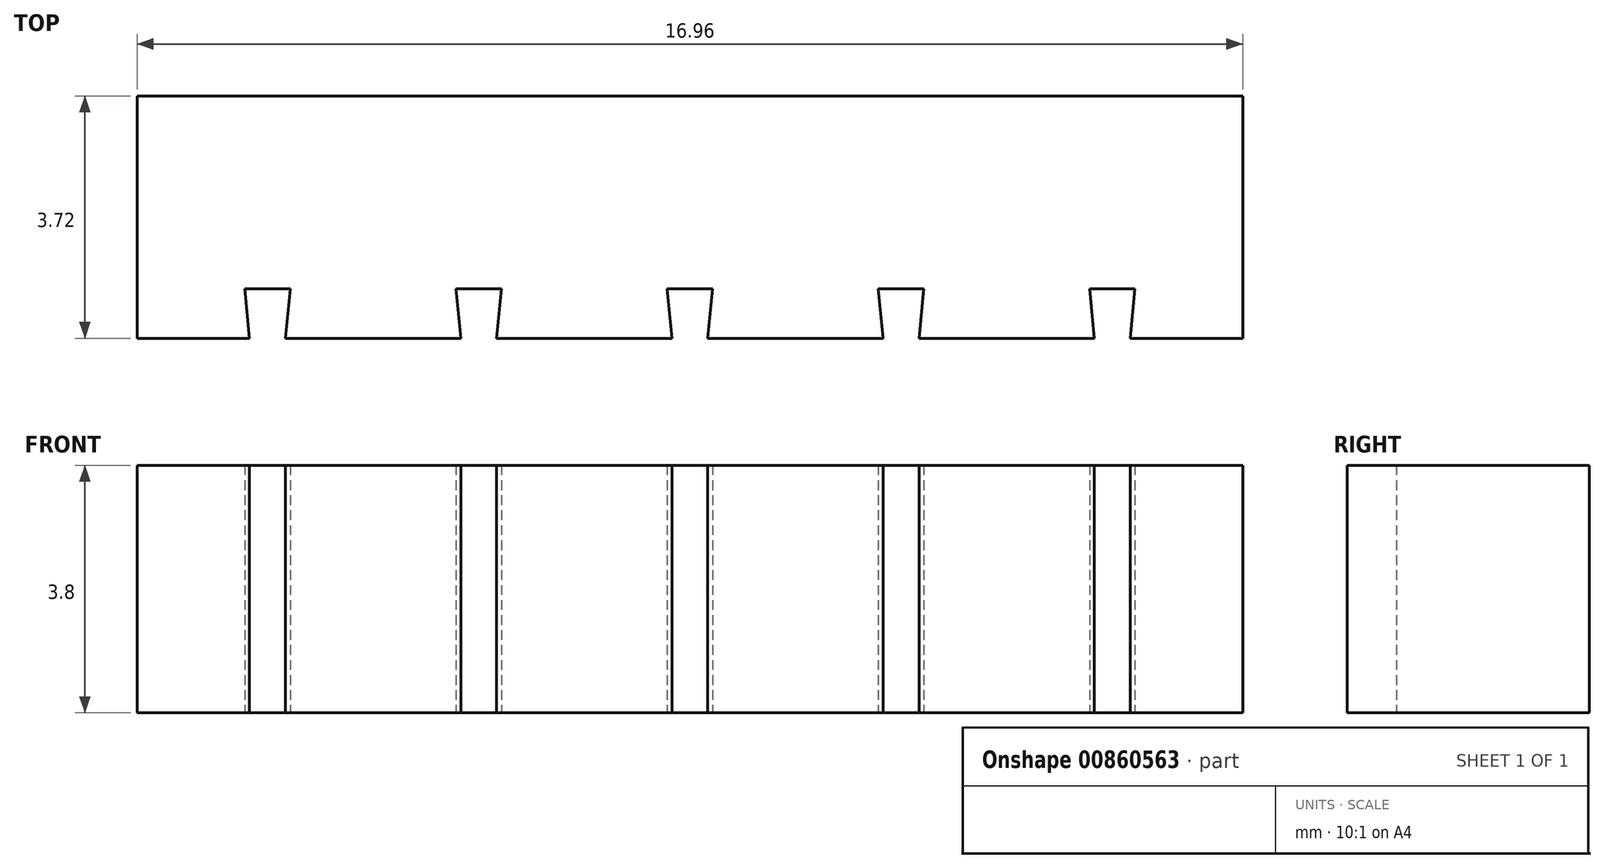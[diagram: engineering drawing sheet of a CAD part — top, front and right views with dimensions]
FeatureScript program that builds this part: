
annotation { "Feature Type Name" : "Feature", "Feature Type Description" : "" }
export const myFeature = defineFeature(function(context is Context, id is Id, definition is map)
    precondition{}
    {
        {
            var Q0;
            Q0=qCreatedBy(makeId("Top.planeOp"),FACE);
            var sketch = newSketch(context, id + "F0", { "sketchPlane" : qUnion([Q0])});
            skLineSegment(sketch, "E0.bottom", {"start": v(0, 0) * mm, "end": v(16.96, 0) * mm});
            skLineSegment(sketch, "E0.top", {"start": v(0, 3.72) * mm, "end": v(16.96, 3.72) * mm});
            skLineSegment(sketch, "E0.left", {"start": v(0, 0) * mm, "end": v(0, 3.72) * mm});
            skLineSegment(sketch, "E0.right", {"start": v(16.96, 0) * mm, "end": v(16.96, 3.72) * mm});
            skLineSegment(sketch, "E1", {"start": v(2, 0) * mm, "end": v(2, 3.72) * mm, "construction": true});
            skLineSegment(sketch, "E2", {"start": v(5.24, 0) * mm, "end": v(5.24, 3.72) * mm, "construction": true});
            skLineSegment(sketch, "E3", {"start": v(8.48, 3.72) * mm, "end": v(8.48, 0) * mm, "construction": true});
            skLineSegment(sketch, "E4", {"start": v(11.72, 0) * mm, "end": v(11.72, 3.72) * mm, "construction": true});
            skLineSegment(sketch, "E5", {"start": v(14.96, 3.72) * mm, "end": v(14.96, 0) * mm, "construction": true});
            skLineSegment(sketch, "E6", {"start": v(5.24, 0) * mm, "end": v(8.48, 0) * mm});
            skLineSegment(sketch, "E7", {"start": v(11.72, 0) * mm, "end": v(14.96, 0) * mm});
            skLineSegment(sketch, "E8", {"start": v(2, 0) * mm, "end": v(5.24, 0) * mm});
            skLineSegment(sketch, "E9", {"start": v(8.48, 0) * mm, "end": v(11.72, 0) * mm});
            skLineSegment(sketch, "E10", {"start": v(0, 0) * mm, "end": v(2, 0) * mm});
            skLineSegment(sketch, "E11", {"start": v(14.96, 0) * mm, "end": v(16.96, 0) * mm});
            skLineSegment(sketch, "E12", {"start": v(0, 0.76) * mm, "end": v(16.96, 0.76) * mm, "construction": true});
            skLineSegment(sketch, "E13", {"start": v(1.73, 0) * mm, "end": v(1.65, 0.76) * mm});
            skLineSegment(sketch, "E14", {"start": v(1.65, 0.76) * mm, "end": v(2, 0.76) * mm});
            skLineSegment(sketch, "E15", {"start": v(2, 0.76) * mm, "end": v(2.35, 0.76) * mm});
            skLineSegment(sketch, "E16", {"start": v(2.35, 0.76) * mm, "end": v(2.27, 0) * mm});
            skLineSegment(sketch, "E17", {"start": v(4.97, 0) * mm, "end": v(4.9, 0.76) * mm});
            skLineSegment(sketch, "E18", {"start": v(4.9, 0.76) * mm, "end": v(5.24, 0.76) * mm});
            skLineSegment(sketch, "E19", {"start": v(5.24, 0.76) * mm, "end": v(5.59, 0.76) * mm});
            skLineSegment(sketch, "E20", {"start": v(5.59, 0.76) * mm, "end": v(5.51, 0) * mm});
            skLineSegment(sketch, "E21", {"start": v(1.73, 0) * mm, "end": v(2.27, 0) * mm});
            skLineSegment(sketch, "E22", {"start": v(4.97, 0) * mm, "end": v(5.52, 0) * mm});
            skLineSegment(sketch, "E23", {"start": v(8.2, 0) * mm, "end": v(8.13, 0.76) * mm});
            skLineSegment(sketch, "E24", {"start": v(8.13, 0.76) * mm, "end": v(8.48, 0.76) * mm});
            skLineSegment(sketch, "E25", {"start": v(8.48, 0.76) * mm, "end": v(8.83, 0.76) * mm});
            skLineSegment(sketch, "E26", {"start": v(8.83, 0.76) * mm, "end": v(8.75, 0) * mm});
            skLineSegment(sketch, "E27", {"start": v(8.76, 0) * mm, "end": v(8.2, 0) * mm});
            skLineSegment(sketch, "E28", {"start": v(11.45, 0) * mm, "end": v(11.37, 0.76) * mm});
            skLineSegment(sketch, "E29", {"start": v(11.37, 0.76) * mm, "end": v(11.72, 0.76) * mm});
            skLineSegment(sketch, "E30", {"start": v(11.72, 0.76) * mm, "end": v(12.07, 0.76) * mm});
            skLineSegment(sketch, "E31", {"start": v(12.07, 0.76) * mm, "end": v(12, 0) * mm});
            skLineSegment(sketch, "E32", {"start": v(12, 0) * mm, "end": v(11.45, 0) * mm});
            skLineSegment(sketch, "E33", {"start": v(14.69, 0) * mm, "end": v(14.61, 0.76) * mm});
            skLineSegment(sketch, "E34", {"start": v(14.61, 0.76) * mm, "end": v(14.96, 0.76) * mm});
            skLineSegment(sketch, "E35", {"start": v(14.96, 0.76) * mm, "end": v(15.3, 0.76) * mm});
            skLineSegment(sketch, "E36", {"start": v(15.3, 0.76) * mm, "end": v(15.24, 0) * mm});
            skLineSegment(sketch, "E37", {"start": v(15.24, 0) * mm, "end": v(14.69, 0) * mm});
            skSolve(sketch);
        }
        {
            var Q0;
            Q0=makeQuery(id+"F0.imprint","IMPRINT",FACE,{"disambiguationData":[TD([[makeQuery(id+"F0.imprint","IMPRINT",EDGE,{"derivedFrom":sQuery(id+"F0.wireOp",EDGE,"E0.top")}),-1.0]])]});
            extrude(context, id + "F1", {"entities" : qUnion([Q0]), "depth" : 3.8 * mm, "offsetDistance" : 25 * mm});
        }
    });
